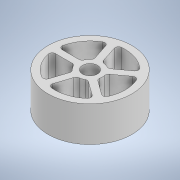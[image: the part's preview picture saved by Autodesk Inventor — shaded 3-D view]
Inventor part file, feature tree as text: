
AUTODESK INVENTOR PART (.ipt)
format: ipt  version: 2020 (Build 240168000, 168)  size: 187,392 bytes
history: native  units: mm
features: extrude x1, fillet x1, pattern_circular x1, sketch x1
ambient origin geometry x8: Origin, YZ Plane, XZ Plane, XY Plane, X Axis, Y Axis, Z Axis, Center Point
bodies: Solid1 (feature_tree)
feature tree (4):
  extrude  "Extrusion1"  Depth=2.0mm
  fillet  "Fillet1"  Radius=3.0mm
  pattern_circular  "Circular Pattern1"  [2 undecoded]
  sketch  "Sketch1"  dims[d0=9.0mm d1=50.0mm d2=3.0mm d3=4.0mm d4=4.0mm d5=20.0mm d6=50.0mm d8=360.0deg d10=21.0mm d11=0.0mm d12=2.0mm d13=50.0mm d14=360.0deg]
note: 2 required parameter values undecoded (feature->parameter linkage not recoverable at this tier; creation-order binding heuristic only, values carry confidence <= 0.55)
